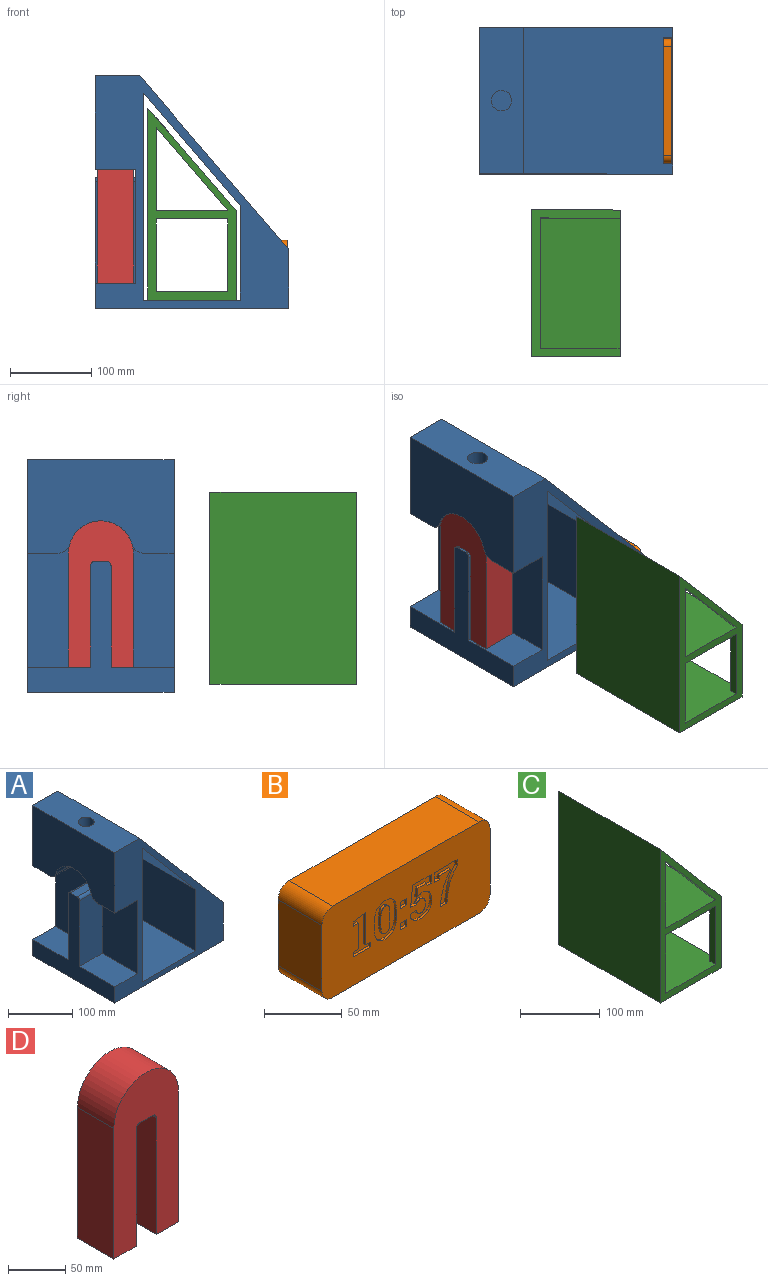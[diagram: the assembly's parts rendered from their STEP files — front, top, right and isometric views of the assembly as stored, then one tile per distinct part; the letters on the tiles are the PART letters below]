
ASSEMBLY  parts=4 mates=3
PART A: 32 faces, bbox 238.3x180x285.8 mm
  f0: plane 285.83x238.29mm, normal (0,-1,0), area 19555.8mm2, adj f2,f3,f4,f5,f6,f7,f21,f22
  f1: plane 285.83x238.29mm, normal (0,1,0), area 19555.8mm2, adj f2,f3,f4,f5,f6,f7,f14,f15
  f2: plane 180x160.83mm, normal (-1,0,0), area 8789.3mm2, adj f0,f1,f6,f15,f16,f17,f18,f19
  f3: plane 213.83x183.29mm, normal (0.76,0,0.65), area 48040.4mm2, adj f0,f1,f4,f7,f8,f10,f11
  f4: plane 180x55mm, normal (0,0,1), area 9409.1mm2, adj f0,f1,f3,f5,f26
  f5: plane 180x115mm, normal (-1,0,0), area 18126.2mm2, adj f0,f1,f4,f13,f14,f22,f24,f25
  f6: plane 238.29x180mm, normal (0,0,-1), area 42891.4mm2, adj f0,f1,f2,f7
  f7: plane 180x72mm, normal (1,0,0), area 3350mm2, adj f0,f1,f3,f6,f8,f9,f10
  f8: plane 75x42mm, normal (0,1,0), area 3077.6mm2, adj f3,f7,f9,f11,f12
  f9: plane 155x42mm, normal (0,0,1), area 6510mm2, adj f7,f8,f10,f12
  f10: plane 75x42mm, normal (0,-1,0), area 3077.6mm2, adj f3,f7,f9,f11,f12
  f11: plane 155x30.86mm, normal (0,0,-1), area 4782.9mm2, adj f3,f8,f10,f12
  f12: plane 155x75mm, normal (1,0,0), area 11625mm2, adj f8,f9,f10,f11
  f13: cylinder r=40mm len=76.97mm, axis (-1,0,0), area 5178.3mm2, adj f5,f23,f24,f25
  f14: plane 50x37.09mm, normal (0,0,-1), area 1854.2mm2, adj f1,f5,f23,f25
  f15: plane 77.5x50mm, normal (0,0,1), area 3875mm2, adj f1,f2,f16,f23
  f16: plane 125x50mm, normal (0,1,0), area 6250mm2, adj f2,f15,f17,f23
  f17: cylinder r=5mm len=50mm, axis (-1,0,0), area 392.7mm2, adj f2,f16,f18,f23
  f18: plane 50x15mm, normal (0,0,1), area 750mm2, adj f2,f17,f19,f23
  f19: cylinder r=5mm len=50mm, axis (-1,0,0), area 392.7mm2, adj f2,f18,f20,f23
  f20: plane 125x50mm, normal (0,-1,0), area 6250mm2, adj f2,f19,f21,f23
  f21: plane 77.5x50mm, normal (0,0,1), area 3875mm2, adj f0,f2,f20,f23
  f22: plane 50x37.09mm, normal (0,0,-1), area 1854.2mm2, adj f0,f5,f23,f24
  f23: plane 180x180mm, normal (-1,0,0), area 24534.5mm2, adj f0,f1,f13,f14,f15,f16,f17,f18
  f24: cylinder r=15mm len=50mm, axis (-1,0,0), area 970.9mm2, adj f5,f13,f22,f23
  f25: cylinder r=15mm len=50mm, axis (-1,0,0), area 970.9mm2, adj f5,f13,f14,f23
  f26: cylinder r=12.5mm len=25mm, axis (0,0,1), area 1963.5mm2, adj f4,f27
  f27: plane 25x25mm, normal (0,0,1), area 490.9mm2, adj f26
  f28: plane 180x116.63mm, normal (-1,0,0), area 20994.1mm2, adj f0,f1,f29,f31
  f29: plane 180x138mm, normal (-0.76,0,-0.65), area 32716.2mm2, adj f0,f1,f28,f30
  f30: plane 254.63x180mm, normal (1,0,0), area 45834.1mm2, adj f0,f1,f29,f31
  f31: plane 180x118.29mm, normal (0,0,1), area 21291.4mm2, adj f0,f1,f28,f30
PART B: 94 faces, bbox 153x40x72 mm
  f0: plane 153x72mm, normal (0,-1,0), area 9507.9mm2, adj f1,f2,f3,f4,f5,f6,f7,f8
  f1: plane 52x40mm, normal (-1,0,0), area 2080mm2, adj f0,f2,f8,f9
  f2: cylinder r=10mm len=40mm, axis (0,1,0), area 628.3mm2, adj f0,f1,f3,f9
  f3: plane 133x40mm, normal (0,0,-1), area 5320mm2, adj f0,f2,f4,f9
  f4: cylinder r=10mm len=40mm, axis (0,1,0), area 628.3mm2, adj f0,f3,f5,f9
  f5: plane 52x40mm, normal (1,0,0), area 2080mm2, adj f0,f4,f6,f9
  f6: cylinder r=10mm len=40mm, axis (0,1,0), area 628.3mm2, adj f0,f5,f7,f9
  f7: plane 133x40mm, normal (0,0,1), area 5320mm2, adj f0,f6,f8,f9
  f8: cylinder r=10mm len=40mm, axis (0,1,0), area 628.3mm2, adj f0,f1,f7,f9
  f9: plane 153x72mm, normal (0,1,0), area 10930.2mm2, adj f1,f2,f3,f4,f5,f6,f7,f8
  f10: plane 6.53x2mm, normal (-1,0,0), area 13.1mm2, adj f0,f11,f29,f30
  f11: extruded ~8.92x2.72mm, area 19.1mm2, adj f0,f10,f12,f30
  f12: extruded ~7.31x3.06mm, area 16.4mm2, adj f0,f11,f13,f30
  f13: extruded ~7.32x3.06mm, area 16.4mm2, adj f0,f12,f14,f30
  f14: extruded ~8.92x2.7mm, area 19.1mm2, adj f0,f13,f15,f30
  f15: plane 6.53x2mm, normal (1,0,0), area 13.1mm2, adj f0,f14,f16,f30
  f16: extruded ~8.92x2.71mm, area 19.1mm2, adj f0,f15,f17,f30
  f17: extruded ~7.35x3.04mm, area 16.4mm2, adj f0,f16,f18,f30
  f18: extruded ~7.29x3.04mm, area 16.3mm2, adj f0,f17,f29,f30
  f19: plane 7.72x2mm, normal (1,0,0), area 15.4mm2, adj f20,f28,f30,f31
  f20: extruded ~5.21x2mm, area 10.8mm2, adj f19,f21,f30,f31
  f21: extruded ~3.03x2mm, area 7.2mm2, adj f20,f22,f30,f31
  f22: extruded ~3.08x2mm, area 7.3mm2, adj f21,f23,f30,f31
  f23: extruded ~5.21x2mm, area 10.8mm2, adj f22,f24,f30,f31
  f24: plane 7.72x2mm, normal (-1,0,0), area 15.4mm2, adj f23,f25,f30,f31
  f25: extruded ~5.17x2mm, area 10.7mm2, adj f24,f26,f30,f31
  f26: extruded ~3.05x2mm, area 7.3mm2, adj f25,f27,f30,f31
  f27: extruded ~3.05x2mm, area 7.3mm2, adj f26,f28,f30,f31
  f28: extruded ~5.16x2mm, area 10.7mm2, adj f19,f27,f30,f31
  f29: extruded ~8.92x2.7mm, area 19.1mm2, adj f0,f10,f18,f30
  f30: plane 30.48x20.04mm, normal (0,-1,0), area 368.1mm2, adj f10,f11,f12,f13,f14,f15,f16,f17
  f31: plane 21.35x8.2mm, normal (0,-1,0), area 156.7mm2, adj f19,f20,f21,f22,f23,f24,f25,f26
  f32: plane 4.58x2mm, normal (-1,0,0), area 9.2mm2, adj f0,f33,f44,f45
  f33: plane 20.94x2mm, normal (0,0,-1), area 41.9mm2, adj f0,f32,f34,f45
  f34: plane 7.51x2mm, normal (1,0,0), area 15mm2, adj f0,f33,f35,f45
  f35: plane 4.56x2mm, normal (0,0,1), area 9.1mm2, adj f0,f34,f36,f45
  f36: plane 2.93x2mm, normal (-1,0,0.08), area 5.9mm2, adj f0,f35,f37,f45
  f37: plane 10.44x2mm, normal (0,0,1), area 20.9mm2, adj f0,f36,f38,f45
  f38: extruded ~10.04x6.25mm, area 23.8mm2, adj f0,f37,f39,f45
  f39: extruded ~11.99x2.97mm, area 24.8mm2, adj f0,f38,f40,f45
  f40: plane 3.01x2mm, normal (1,0,-0.09), area 6.1mm2, adj f0,f39,f41,f45
  f41: plane 5.94x2mm, normal (0,0,1), area 11.9mm2, adj f0,f40,f42,f45
  f42: plane 3.01x2mm, normal (-1,0,0.09), area 6.1mm2, adj f0,f41,f43,f45
  f43: extruded ~11.63x2.49mm, area 23.8mm2, adj f0,f42,f44,f45
  f44: extruded ~10.4x6.5mm, area 24.7mm2, adj f0,f32,f43,f45
  f45: plane 29.62x20.94mm, normal (0,-1,0), area 253.9mm2, adj f32,f33,f34,f35,f36,f37,f38,f39
  f46: plane 3.67x2mm, normal (0,0,1), area 7.3mm2, adj f0,f47,f71,f72
  f47: plane 6.75x2mm, normal (-1,0,0), area 13.5mm2, adj f0,f46,f48,f72
  f48: plane 17.05x2mm, normal (0,0,-1), area 34.1mm2, adj f0,f47,f49,f72
  f49: plane 16.5x2mm, normal (0.99,0,-0.1), area 33.2mm2, adj f0,f48,f50,f72
  f50: plane 5.25x2mm, normal (0.07,0,1), area 10.5mm2, adj f0,f49,f51,f72
  f51: extruded ~2x1.71mm, area 4.3mm2, adj f0,f50,f52,f72
  f52: extruded ~2.6x2mm, area 5.4mm2, adj f0,f51,f53,f72
  f53: extruded ~3.15x2mm, area 7.3mm2, adj f0,f52,f54,f72
  f54: extruded ~4.11x2mm, area 8.6mm2, adj f0,f53,f55,f72
  f55: extruded ~3.84x2mm, area 8.1mm2, adj f0,f54,f56,f72
  f56: extruded ~3.07x2mm, area 7.1mm2, adj f0,f55,f57,f72
  f57: extruded ~2.93x2mm, area 6.4mm2, adj f0,f56,f58,f72
  f58: extruded ~3.08x2mm, area 6.7mm2, adj f0,f57,f59,f72
  f59: plane 5.7x2mm, normal (0.05,0,-1), area 11.4mm2, adj f0,f58,f60,f72
  f60: plane 2x0.1mm, normal (0.91,0,-0.42), area 0.2mm2, adj f0,f59,f61,f72
  f61: extruded ~6.14x2.82mm, area 14.1mm2, adj f0,f60,f62,f72
  f62: extruded ~6.98x2.23mm, area 14.9mm2, adj f0,f61,f63,f72
  f63: extruded ~7.41x2.83mm, area 16.4mm2, adj f0,f62,f64,f72
  f64: extruded ~7.1x2.58mm, area 15.5mm2, adj f0,f63,f65,f72
  f65: extruded ~7.37x2.34mm, area 15.8mm2, adj f0,f64,f66,f72
  f66: extruded ~6.61x2.59mm, area 14.7mm2, adj f0,f65,f67,f72
  f67: extruded ~2.57x2mm, area 5.2mm2, adj f0,f66,f68,f72
  f68: extruded ~2x1.99mm, area 4.5mm2, adj f0,f67,f69,f72
  f69: plane 6.84x2mm, normal (-0.99,0,0.12), area 13.8mm2, adj f0,f68,f70,f72
  f70: plane 7.98x2mm, normal (0,0,1), area 16mm2, adj f0,f69,f71,f72
  f71: plane 2x1.99mm, normal (0.97,0,0.26), area 4.1mm2, adj f0,f46,f70,f72
  f72: plane 30.05x19.88mm, normal (0,-1,0), area 351.5mm2, adj f46,f47,f48,f49,f50,f51,f52,f53
  f73: plane 5.21x2mm, normal (-1,0,0), area 10.4mm2, adj f0,f74,f76,f77
  f74: plane 5.92x2mm, normal (0,0,-1), area 11.8mm2, adj f0,f73,f75,f77
  f75: plane 5.21x2mm, normal (1,0,0), area 10.4mm2, adj f0,f74,f76,f77
  f76: plane 5.92x2mm, normal (0,0,1), area 11.8mm2, adj f0,f73,f75,f77
  f77: plane 5.92x5.21mm, normal (0,-1,0), area 30.9mm2, adj f73,f74,f75,f76
  f78: plane 5.21x2mm, normal (-1,0,0), area 10.4mm2, adj f0,f79,f81,f82
  f79: plane 5.92x2mm, normal (0,0,-1), area 11.8mm2, adj f0,f78,f80,f82
  f80: plane 5.21x2mm, normal (1,0,0), area 10.4mm2, adj f0,f79,f81,f82
  f81: plane 5.92x2mm, normal (0,0,1), area 11.8mm2, adj f0,f78,f80,f82
  f82: plane 5.92x5.21mm, normal (0,-1,0), area 30.9mm2, adj f78,f79,f80,f81
  f83: plane 3.56x2mm, normal (1,0,0), area 7.1mm2, adj f0,f84,f92,f93
  f84: plane 15.93x2mm, normal (0,0,1), area 31.9mm2, adj f0,f83,f85,f93
  f85: plane 3.56x2mm, normal (-1,0,0), area 7.1mm2, adj f0,f84,f86,f93
  f86: plane 5.01x2mm, normal (-0.12,0,-0.99), area 10.1mm2, adj f0,f85,f87,f93
  f87: plane 25.45x2mm, normal (-1,0,0), area 50.9mm2, adj f0,f86,f88,f93
  f88: plane 10.98x2mm, normal (0.18,0,-0.98), area 22.3mm2, adj f0,f87,f89,f93
  f89: plane 3.4x2mm, normal (1,0,0), area 6.8mm2, adj f0,f88,f90,f93
  f90: plane 5.07x2mm, normal (0,0,1), area 10.1mm2, adj f0,f89,f91,f93
  f91: plane 20.06x2mm, normal (1,0,0), area 40.1mm2, adj f0,f90,f92,f93
  f92: plane 5.01x2mm, normal (0.12,0,-0.99), area 10.1mm2, adj f0,f83,f91,f93
  f93: plane 29.62x15.99mm, normal (0,-1,0), area 230.4mm2, adj f83,f84,f85,f86,f87,f88,f89,f90
PART C: 19 faces, bbox 108.3x180x236.1 mm
  f0: plane 180x109.78mm, normal (1,0,0), area 5395.7mm2, adj f2,f3,f4,f6,f8,f10,f11,f17
  f1: plane 89.78x10mm, normal (-1,0,0), area 897.8mm2, adj f2,f8,f10,f17
  f2: plane 236.12x108.29mm, normal (0,-1,0), area 6254.7mm2, adj f0,f1,f4,f5,f6,f8,f9,f10
  f3: plane 236.12x108.29mm, normal (0,1,0), area 6254.7mm2, adj f0,f4,f5,f6,f7,f8,f9,f10
  f4: plane 180x126.33mm, normal (0.76,0,0.65), area 5856.6mm2, adj f0,f2,f3,f5,f14,f15,f16
  f5: plane 236.12x180mm, normal (-1,0,0), area 42501.2mm2, adj f2,f3,f4,f6
  f6: plane 180x108.29mm, normal (0,0,-1), area 19491.4mm2, adj f0,f2,f3,f5
  f7: plane 89.78x10mm, normal (-1,0,0), area 897.8mm2, adj f3,f8,f10,f18
  f8: plane 180x98.29mm, normal (0,0,-1), area 17491.4mm2, adj f0,f1,f2,f3,f7,f9,f17,f18
  f9: plane 180x89.78mm, normal (1,0,0), area 16161.2mm2, adj f2,f3,f8,f10
  f10: plane 180x98.29mm, normal (0,0,1), area 17491.4mm2, adj f0,f1,f2,f3,f7,f9,f17,f18
  f11: plane 180x98.29mm, normal (0,0,1), area 17491.4mm2, adj f0,f2,f3,f12,f13,f14,f15
  f12: plane 180x103mm, normal (-0.76,0,-0.65), area 2783.4mm2, adj f2,f3,f11,f13,f14,f15,f16
  f13: plane 180x103mm, normal (1,0,0), area 18540mm2, adj f2,f3,f11,f12
  f14: plane 114.33x98mm, normal (0,-1,0), area 1085mm2, adj f4,f11,f12,f16
  f15: plane 114.33x98mm, normal (0,1,0), area 1085mm2, adj f4,f11,f12,f16
  f16: plane 160x11.67mm, normal (1,0,0), area 1866.7mm2, adj f4,f12,f14,f15
  f17: plane 89.78x10mm, normal (0,1,0), area 897.8mm2, adj f0,f1,f8,f10
  f18: plane 89.78x10mm, normal (0,-1,0), area 897.8mm2, adj f0,f7,f8,f10
PART D: 12 faces, bbox 80x45x180 mm
  f0: plane 45x27.5mm, normal (0,0,-1), area 1237.5mm2, adj f1,f9,f10,f11
  f1: plane 125x45mm, normal (1,0,0), area 5625mm2, adj f0,f2,f10,f11
  f2: cylinder r=5mm len=45mm, axis (0,1,0), area 353.4mm2, adj f1,f3,f10,f11
  f3: plane 45x15mm, normal (0,0,-1), area 675mm2, adj f2,f4,f10,f11
  f4: cylinder r=5mm len=45mm, axis (0,1,0), area 353.4mm2, adj f3,f5,f10,f11
  f5: plane 125x45mm, normal (-1,0,0), area 5625mm2, adj f4,f6,f10,f11
  f6: plane 45x27.5mm, normal (0,0,-1), area 1237.5mm2, adj f5,f7,f10,f11
  f7: plane 140x45mm, normal (1,0,0), area 6300mm2, adj f6,f8,f10,f11
  f8: cylinder r=40mm len=80mm, axis (0,1,0), area 5654.9mm2, adj f7,f9,f10,f11
  f9: plane 140x45mm, normal (-1,0,0), area 6300mm2, adj f0,f8,f10,f11
  f10: plane 180x80mm, normal (0,-1,0), area 10474mm2, adj f0,f1,f2,f3,f4,f5,f6,f7
  f11: plane 180x80mm, normal (0,1,0), area 10474mm2, adj f0,f1,f2,f3,f4,f5,f6,f7
PLACE A t=(-115.97,73.33,-35.68)mm fixed
PLACE B rot(axis=(0,0,1),90deg) t=(80.32,73.33,11.82)mm
PLACE C t=(23.08,-60.89,54.97)mm
PLACE D rot(axis=(0,0,1),90deg) t=(-113.47,73.33,85.16)mm
MATE fastened B.f9 <-> A.f12  axis (-1,0,0) through (80.32,73.33,11.82)mm
MATE planar C.f6 <-> A.f31  axis (0,0,-1) through (3.18,-150.89,-25.68)mm
MATE fastened D.f3 <-> A.f18  axis (0,0,-1) through (-90.97,73.33,125.16)mm
